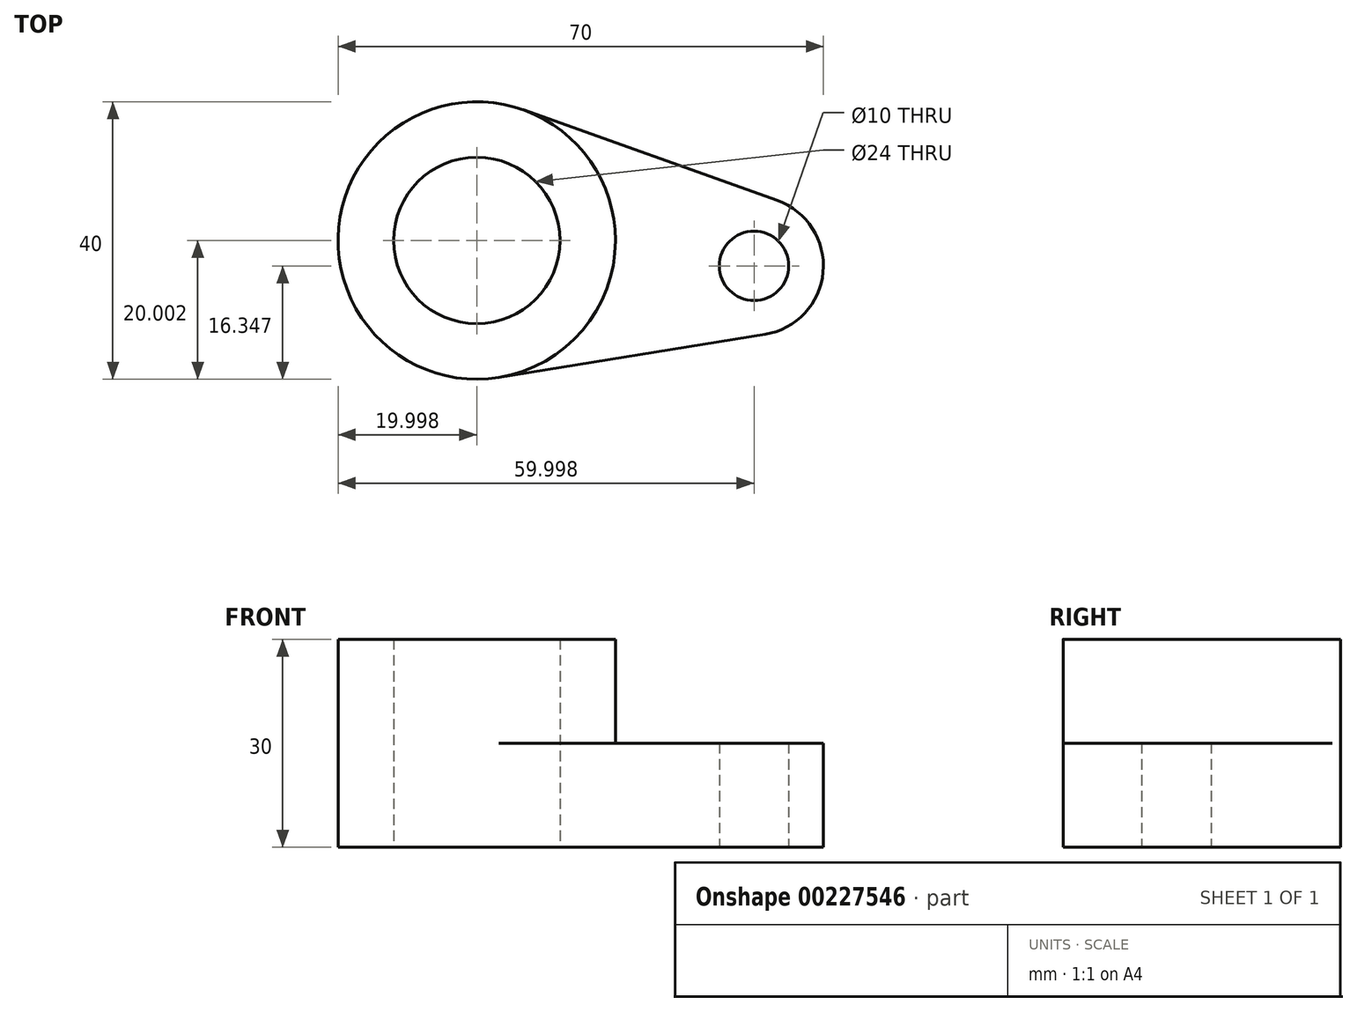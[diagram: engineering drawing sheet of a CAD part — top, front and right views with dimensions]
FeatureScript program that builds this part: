
annotation { "Feature Type Name" : "Feature", "Feature Type Description" : "" }
export const myFeature = defineFeature(function(context is Context, id is Id, definition is map)
    precondition{}
    {
        {
            var Q0;
            Q0=qCreatedBy(makeId("Top.planeOp"),FACE);
            var sketch = newSketch(context, id + "F0", { "sketchPlane" : qUnion([Q0])});
            skCircle(sketch, "E0", {"center": v(-36.54, 32.21) * mm, "radius": 20 * mm});
            skArc(sketch, "E1", {"start": v(5.06, 18.69) * mm, "mid": v(13.42, 27.65) * mm, "end": v(6.82, 37.98) * mm});
            skCircle(sketch, "E2", {"center": v(-36.54, 32.21) * mm, "radius": 12 * mm});
            skCircle(sketch, "E3", {"center": v(3.46, 28.56) * mm, "radius": 5 * mm});
            skLineSegment(sketch, "E4", {"start": v(-29.82, 51.05) * mm, "end": v(6.82, 37.98) * mm});
            skLineSegment(sketch, "E5", {"start": v(-33.35, 12.47) * mm, "end": v(5.06, 18.69) * mm});
            skSolve(sketch);
        }
        {
            var Q0;
            Q0=makeQuery(id+"F0.imprint","IMPRINT",FACE,{"disambiguationData":[TD([[makeQuery(id+"F0.imprint","IMPRINT",EDGE,{"derivedFrom":sQuery(id+"F0.wireOp",EDGE,"E1")}),1.0]])]});
            extrude(context, id + "F1", {"entities" : qUnion([Q0]), "depth" : 15 * mm});
        }
        {
            var Q0;
            Q0=makeQuery(id+"F0.imprint","IMPRINT",FACE,{"disambiguationData":[TD([[makeQuery(id+"F0.imprint","IMPRINT",EDGE,{"derivedFrom":sQuery(id+"F0.wireOp",EDGE,"E2")}),-1.0]])]});
            extrude(context, id + "F2", {"entities" : qUnion([Q0]), "operationType" : NewBodyOperationType.ADD, "depth" : 30 * mm});
        }
    });
